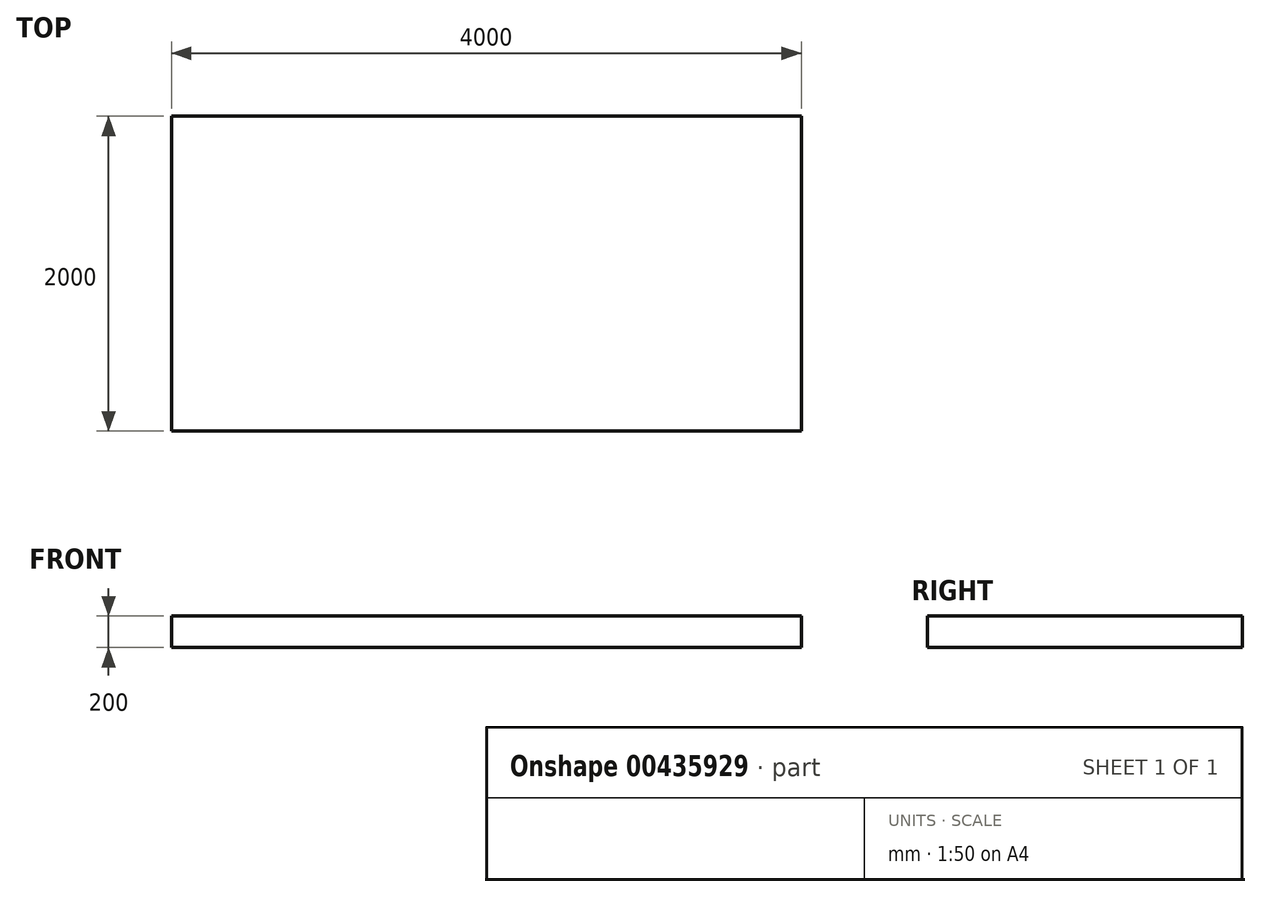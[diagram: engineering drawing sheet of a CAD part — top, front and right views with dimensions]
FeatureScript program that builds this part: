
annotation { "Feature Type Name" : "Feature", "Feature Type Description" : "" }
export const myFeature = defineFeature(function(context is Context, id is Id, definition is map)
    precondition{}
    {
        {
            var Q0;
            Q0=qCreatedBy(makeId("Top.planeOp"),FACE);
            var sketch = newSketch(context, id + "F0", { "sketchPlane" : qUnion([Q0])});
            skLineSegment(sketch, "E0.bottom", {"start": v(2000, -1000) * mm, "end": v(-2000, -1000) * mm});
            skLineSegment(sketch, "E0.top", {"start": v(2000, 1000) * mm, "end": v(-2000, 1000) * mm});
            skLineSegment(sketch, "E0.left", {"start": v(2000, -1000) * mm, "end": v(2000, 1000) * mm});
            skLineSegment(sketch, "E0.right", {"start": v(-2000, -1000) * mm, "end": v(-2000, 1000) * mm});
            skPoint(sketch, "E0.middle", {"position": v(0, 0) * mm});
            skSolve(sketch);
        }
        {
            var Q0;
            Q0=makeQuery(id+"F0.imprint","IMPRINT",FACE,{"disambiguationData":[TD([[makeQuery(id+"F0.imprint","IMPRINT",EDGE,{"derivedFrom":sQuery(id+"F0.wireOp",EDGE,"E0.bottom")}),-1.0]])]});
            extrude(context, id + "F1", {"entities" : qUnion([Q0]), "depth" : 200 * mm});
        }
    });
